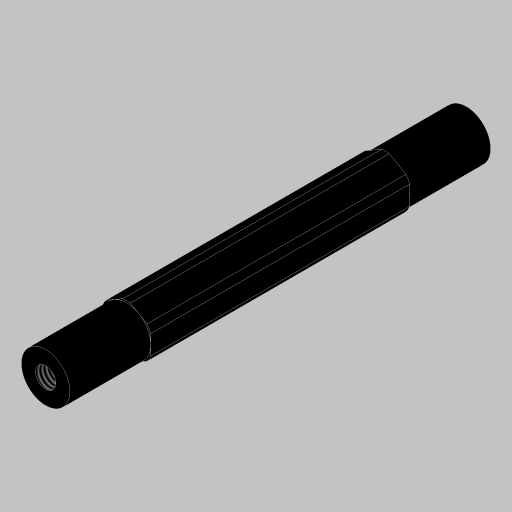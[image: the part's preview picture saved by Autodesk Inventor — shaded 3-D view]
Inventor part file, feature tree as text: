
AUTODESK INVENTOR PART (.ipt)
format: ipt  version: 2023.5 (Build 275446000, 446)  size: 181,248 bytes
history: native  units: in
note: dims shown in document units (in); Inventor stores cm internally (conversion verified against a paired STEP export)
features: extrude x3, projected_geometry x3, hole x1, mirror x1, sketch x1
ambient origin geometry x8: Origin, YZ Plane, XZ Plane, XY Plane, X Axis, Y Axis, Z Axis, Center Point
bodies: Solid1 (feature_tree)
feature tree (9):
  extrude  "Extrusion1"  Depth=0.375in
  hole  "Hole1"  [1 undecoded]
  extrude  "Extrusion3"  Depth=0.625in TaperAngle=0.0deg
  extrude  "Extrusion4"  Depth=0.375in
  mirror  "Mirror2"
  sketch  "Sketch5"  dims[d2=0.0in d9=0.38in d10=0.385in d11=0.25in d12=0.5635in d13=1.0in d14=0.8108in d16=0.7in d17=0.0in d18=0.0in d19=0.625in d20=0.0in d21=0.375in d22=0.5in d23=0.0344in d24=0.5in d25=0.0344in]
  projected_geometry  "Projected Loop2"
  projected_geometry  "Project Cut Edges1"
  projected_geometry  "Project Cut Edges2"
note: 1 required parameter value undecoded (feature->parameter linkage not recoverable at this tier; creation-order binding heuristic only, values carry confidence <= 0.55)
